# Revit family: MR_ОсветительныйПрибор_Perla_soft_КруглойФормы
name_source: partatom
category: Осветительные приборы
units: mm (PartAtom-declared; Revit-internal decimal feet)

## family parameters
Источник света = Да
Общий = Нет
Основа = Грань
При загрузке вырезать с полостями = Нет
Размер круглого соединителя = Использовать диаметр
Тип детали = Нормальный
Точка расчета площади = Нет

## types (1)
- Perla_Soft_КруглойФормы_16w_3000k
    ADSK_URL страницы изделия = https://martinirus.ru
    ADSK_Группирование = Внутреннее освещение-светильник
    ADSK_Единица измерения = шт.
    ADSK_Завод-изготовитель = MartiniRUS
    ADSK_Классификация нагрузок = Освещение
    ADSK_Код изделия = P656933__WW
    ADSK_Количество = 1
    ADSK_Количество фаз = 1
    ADSK_Количество фаз числовое = 1
    ADSK_Коэффициент мощности = 0.98
    ADSK_Масса = 0.5
    ADSK_Материал = <По категории>
    ADSK_Наименование = Perla_Soft_КруглойФормы_16w_3000k
    ADSK_Напряжение = 220 В
    ADSK_Номинальная мощность = 16 В·А
    ADSK_Полная мощность = 16 В·А
    ADSK_Ток = 0 А
    IP Class = IP44
    Группа модели = Perla soft
    Класс Защиты = II
    Описание = Perla soft
    Отметка по умолчанию = 1219 мм
    Полная установленная мощность = 16 В·А
    Самосветящий материал = Источник света по умолчанию
    Светофильтр = 16777215
    Смещение цветовой температуры при затухании лампы = <Нет>
    Угол наклона = 90.00°
    Файл фотометрической сетки = P656933NCWW.ies
